# Revit family: EKF_EE_КаркасВРУ-1UnitS_IP31_PROxima
name_source: partatom
category: Электрооборудование
units: mm (PartAtom-declared; Revit-internal decimal feet)

## family parameters
Всегда вертикально = Нет
На основе рабочей плоскости = Да
Общий = Да
При загрузке вырезать с полостями = Нет
Размер круглого соединителя = Использовать диаметр
Тип детали = Силовой щит
Точка расчета площади = Нет

## types (13) — shared parameters
ADSK_Единица измерения = шт.
ADSK_Завод-изготовитель = EKF
ADSK_Количество = 1
ADSK_Материал = RAL 7035_Сталь
D = 9 мм
t = 1 мм
ВертПроф_Отступ = 30 мм
Изготовитель = EKF
Отступ = 20 мм
РП450 = Вл_EKF_EE_РейкаПоперечнаяUNIT_PROxima : Рейка поперечная для ВРУ Unit глубиной 450мм EKF PROxima
РП600 = Вл_EKF_EE_РейкаПоперечнаяUNIT_PROxima : Рейка поперечная для ВРУ Unit глубиной 600мм EKF PROxima
РП_Отступ = 44 мм
РейкаПопереч_Шаг = 759 мм
Серия номенклатуры = Unit PROxima
Степень защиты IP = IP31
Стойка_a = 24 мм
ТВ = EKF_2
Тип установки = Напольный
zero-valued in all types: ADSK_Масса, Отметка по умолчанию

## per-type parameters (varying)
| type | ADSK_Код изделия | ADSK_Марка | ADSK_Обозначение | ADSK_Размер_Высота | ADSK_Размер_Глубина | ADSK_Размер_Ширина | ЗСтенка_Ширина | РейкаПоперечная | Стойка_h | Тип |
| Каркас ВРУ-1 Unit S сварной (1800х450х450) IP31 EKF PROxima | mb15-04-00m | Каркас ВРУ-1 Unit S | Каркас ВРУ-1 Unit S | 1800 мм | 450 мм | 450 мм | 370 мм | Вл_EKF_EE_РейкаПоперечнаяUNIT_PROxima : Рейка поперечная для ВРУ Unit глубиной 450мм EKF PROxima | 1700 мм | 91 мм |
| Каркас ВРУ-1 Unit S сварной (1800х600х450) IP31 EKF PROxima | mb15-05-00m | Каркас ВРУ-1 Unit S | Каркас ВРУ-1 Unit S | 1800 мм | 450 мм | 600 мм | 520 мм | Вл_EKF_EE_РейкаПоперечнаяUNIT_PROxima : Рейка поперечная для ВРУ Unit глубиной 450мм EKF PROxima | 1700 мм | 92 мм |
| Каркас ВРУ-1 Unit S сварной (1800х600х600) IP31 EKF PROxima | mb-18-60-60n | Каркас ВРУ-1 Unit S | Каркас ВРУ-1 Unit S | 1800 мм | 600 мм | 600 мм | 520 мм | Вл_EKF_EE_РейкаПоперечнаяUNIT_PROxima : Рейка поперечная для ВРУ Unit глубиной 600мм EKF PROxima | 1700 мм | 93 мм |
| Каркас ВРУ-1 Unit S сварной (1800х800х450) IP31 EKF PROxima | mb15-06-00m | Каркас ВРУ-1 Unit S | Каркас ВРУ-1 Unit S | 1800 мм | 450 мм | 800 мм | 720 мм | Вл_EKF_EE_РейкаПоперечнаяUNIT_PROxima : Рейка поперечная для ВРУ Unit глубиной 450мм EKF PROxima | 1700 мм | 94 мм |
| Каркас ВРУ-1 Unit S сварной (1800х800х600) IP31 EKF PROxima | mb-18-80-60n | Каркас ВРУ-1 Unit S | Каркас ВРУ-1 Unit S | 1800 мм | 600 мм | 800 мм | 720 мм | Вл_EKF_EE_РейкаПоперечнаяUNIT_PROxima : Рейка поперечная для ВРУ Unit глубиной 600мм EKF PROxima | 1700 мм | 95 мм |
| Каркас ВРУ-1 Unit S сварной (2000х450х450) IP31 EKF PROxima | mb15-07-00m | Каркас ВРУ-1 Unit S | Каркас ВРУ-1 Unit S | 2000 мм | 450 мм | 450 мм | 370 мм | Вл_EKF_EE_РейкаПоперечнаяUNIT_PROxima : Рейка поперечная для ВРУ Unit глубиной 450мм EKF PROxima | 1900 мм | 96 мм |
| Каркас ВРУ-1 Unit S сварной (2000х600х450) IP31 EKF PROxima | mb15-08-00m | Каркас ВРУ-1 Unit S | Каркас ВРУ-1 Unit S | 2000 мм | 450 мм | 600 мм | 520 мм | Вл_EKF_EE_РейкаПоперечнаяUNIT_PROxima : Рейка поперечная для ВРУ Unit глубиной 450мм EKF PROxima | 1900 мм | 97 мм |
| Каркас ВРУ-1 Unit S сварной (2000х600х600) IP31 EKF PROxima | mb-20-60-60n | Каркас ВРУ-1 Unit S | Каркас ВРУ-1 Unit S | 2000 мм | 600 мм | 600 мм | 520 мм | Вл_EKF_EE_РейкаПоперечнаяUNIT_PROxima : Рейка поперечная для ВРУ Unit глубиной 600мм EKF PROxima | 1900 мм | 98 мм |
| Каркас ВРУ-1 Unit S сварной (2000х800х450) IP31 EKF PROxima | mb15-09-00m | Каркас ВРУ-1 Unit S | Каркас ВРУ-1 Unit S | 2000 мм | 450 мм | 800 мм | 720 мм | Вл_EKF_EE_РейкаПоперечнаяUNIT_PROxima : Рейка поперечная для ВРУ Unit глубиной 450мм EKF PROxima | 1900 мм | 99 мм |
| Каркас ВРУ-1 Unit S сварной (2000х800х600) IP31 EKF PROxima | mb-20-80-60n | Каркас ВРУ-1 Unit S | Каркас ВРУ-1 Unit S | 2000 мм | 600 мм | 800 мм | 720 мм | Вл_EKF_EE_РейкаПоперечнаяUNIT_PROxima : Рейка поперечная для ВРУ Unit глубиной 600мм EKF PROxima | 1900 мм | 100 мм |
| Каркас ВРУ-1 Unit S сварной с внутренней комплектацией (1800х600х450) IP31 EKF PROxima | mb18-60-45k | Каркас ВРУ-1 Unit S с внутренней комплектацией | Каркас ВРУ-1 Unit S с внутренней комплектацией | 1800 мм | 450 мм | 600 мм | 520 мм | Вл_EKF_EE_РейкаПоперечнаяUNIT_PROxima : Рейка поперечная для ВРУ Unit глубиной 450мм EKF PROxima | 1700 мм | 101 мм |
| Каркас ВРУ-1 Unit S сварной с внутренней комплектацией (1800х800х450) IP31 EKF PROxima | mb18-80-45k | Каркас ВРУ-1 Unit S с внутренней комплектацией | Каркас ВРУ-1 Unit S с внутренней комплектацией | 1800 мм | 450 мм | 800 мм | 720 мм | Вл_EKF_EE_РейкаПоперечнаяUNIT_PROxima : Рейка поперечная для ВРУ Unit глубиной 450мм EKF PROxima | 1700 мм | 102 мм |
| Каркас ВРУ-1 Unit S сварной с внутренней комплектацией (2000х600х450) IP31 EKF PROxima | mb20-60-45k | Каркас ВРУ-1 Unit S с внутренней комплектацией | Каркас ВРУ-1 Unit S с внутренней комплектацией | 2000 мм | 450 мм | 600 мм | 520 мм | Вл_EKF_EE_РейкаПоперечнаяUNIT_PROxima : Рейка поперечная для ВРУ Unit глубиной 450мм EKF PROxima | 1900 мм | 103 мм |

note: column(s) folded — value = type name in every type: ADSK_Наименование
